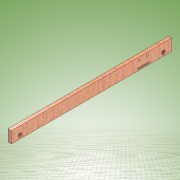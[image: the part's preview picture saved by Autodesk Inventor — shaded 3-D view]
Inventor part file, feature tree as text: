
AUTODESK INVENTOR PART (.ipt)
format: ipt  version: 2022 (Build 260153000, 153)  size: 151,040 bytes
history: native  units: mm
features: extrude x2, sketch x2, other x1
ambient origin geometry x8: Origin, YZ Plane, XZ Plane, XY Plane, X Axis, Y Axis, Z Axis, Center Point
bodies: Body1 (feature_tree)
feature tree (5):
  other  "Sólido1"
  extrude  "Extrusión1"  Depth=280.0mm
  extrude  "Extrusión2"  Depth=6.0mm TaperAngle=0.0deg
  sketch  "Boceto1"  dims[d0=20.0mm d1=280.0mm]
  sketch  "Boceto2"  dims[d2=6.35mm d6=6.0mm d7=0.0mm d8=6.0mm d9=250.0mm d10=15.0mm d11=20.0mm d12=15.0mm d13=40.0mm d14=2.0mm d15=3.0mm d16=2.54mm d17=2.54mm d18=0.0mm d19=0.0mm]
